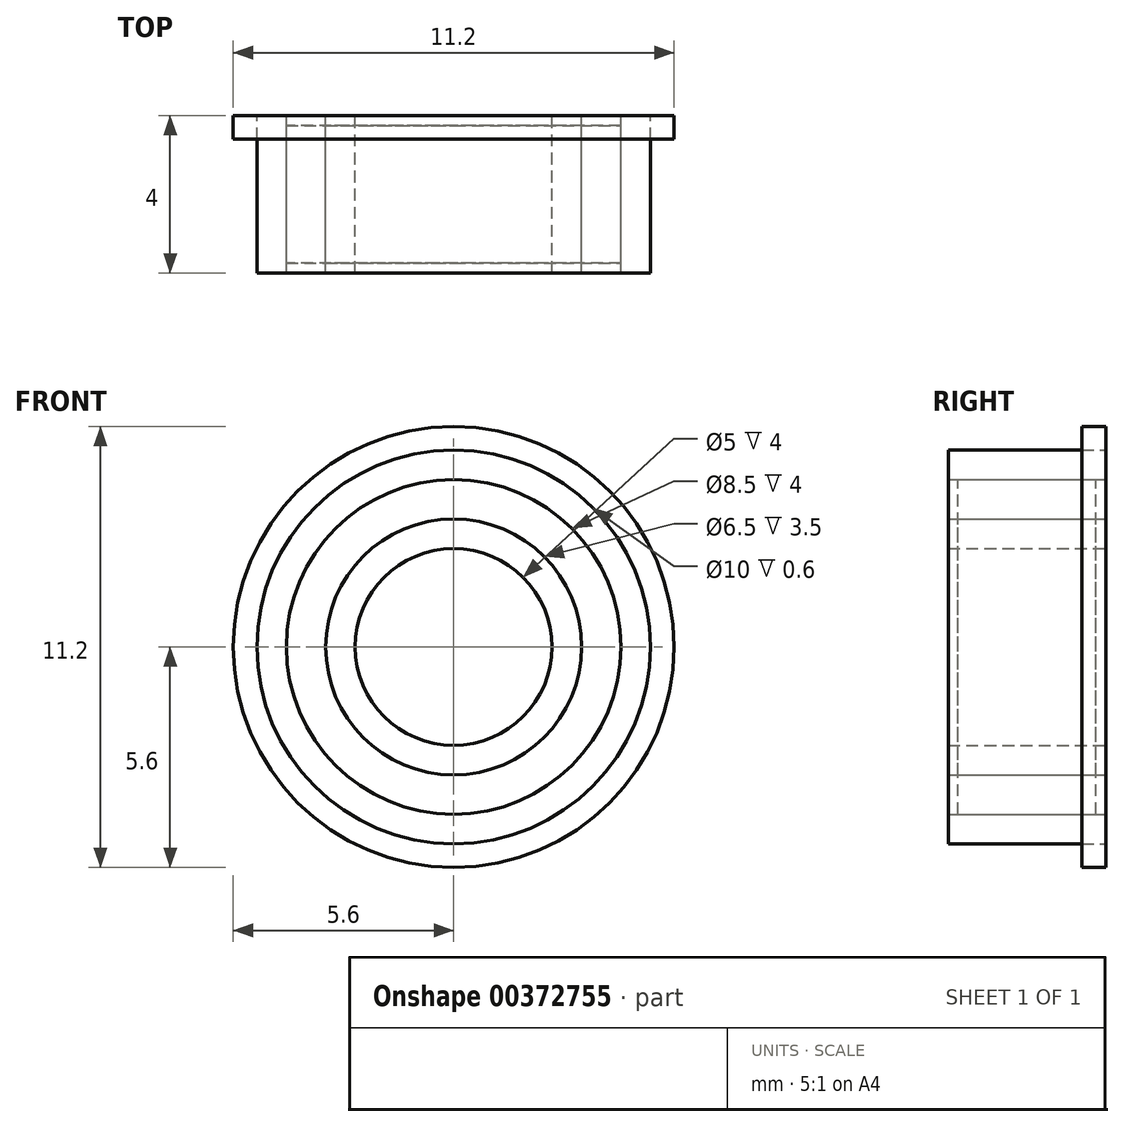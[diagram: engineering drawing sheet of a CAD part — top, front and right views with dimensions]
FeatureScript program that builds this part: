
annotation { "Feature Type Name" : "Feature", "Feature Type Description" : "" }
export const myFeature = defineFeature(function(context is Context, id is Id, definition is map)
    precondition{}
    {
        {
            assignVariable(context, id + "F0", {"name" : "B", "anyValue" : 4});
        }
        {
            assignVariable(context, id + "F1", {"name" : "C1", "anyValue" : 0.6});
        }
        {
            var Q0;
            Q0=qCreatedBy(makeId("Front.planeOp"),FACE);
            var sketch = newSketch(context, id + "F2", { "sketchPlane" : qUnion([Q0])});
            skCircle(sketch, "E0", {"center": v(0, 0) * mm, "radius": 5.6 * mm});
            skCircle(sketch, "E1", {"center": v(0, 0) * mm, "radius": 5 * mm});
            skSolve(sketch);
        }
        {
            var Q0;
            Q0=qSketchRegion(id+"F2",true);
            extrude(context, id + "F3", {"entities" : qUnion([Q0]), "depth" : (getVariable(context, 'C1')) * mm});
        }
        {
            var Q0;
            Q0=qCreatedBy(makeId("Front.planeOp"),FACE);
            var sketch = newSketch(context, id + "F4", { "sketchPlane" : qUnion([Q0])});
            skCircle(sketch, "E2", {"center": v(0, 0) * mm, "radius": 5 * mm});
            skCircle(sketch, "E3", {"center": v(0, 0) * mm, "radius": 4.25 * mm});
            skSolve(sketch);
        }
        {
            var Q0;
            Q0=qSketchRegion(id+"F4",true);
            extrude(context, id + "F5", {"entities" : qUnion([Q0]), "depth" : (getVariable(context, 'B')) * mm});
        }
        {
            var Q0;
            Q0=qCreatedBy(makeId("Front.planeOp"),FACE);
            var sketch = newSketch(context, id + "F6", { "sketchPlane" : qUnion([Q0])});
            skCircle(sketch, "E4", {"center": v(0, 0) * mm, "radius": 2.5 * mm});
            skCircle(sketch, "E5", {"center": v(0, 0) * mm, "radius": 3.25 * mm});
            skSolve(sketch);
        }
        {
            var Q0;
            Q0=qSketchRegion(id+"F6",true);
            extrude(context, id + "F7", {"entities" : qUnion([Q0]), "operationType" : NewBodyOperationType.ADD, "depth" : (getVariable(context, 'B')) * mm});
        }
        {
            var Q0;
            Q0=qCreatedBy(makeId("Front.planeOp"),FACE);
            cPlane(context, id + "F8", {"entities" : qUnion([Q0]), "cplaneType" : CPlaneType.OFFSET, "offset" : (getVariable(context, 'B') / 2) * mm, "width" : 150 * mm, "height" : 150 * mm});
        }
        {
            var Q0;
            Q0=qCreatedBy(id+"F8.planeOp",FACE);
            var sketch = newSketch(context, id + "F9", { "sketchPlane" : qUnion([Q0])});
            skCircle(sketch, "E6", {"center": v(0, 0) * mm, "radius": 3.25 * mm});
            skCircle(sketch, "E7", {"center": v(0, 0) * mm, "radius": 4.25 * mm});
            skSolve(sketch);
        }
        {
            var Q0;
            Q0=qSketchRegion(id+"F9",true);
            extrude(context, id + "F10", {"entities" : qUnion([Q0]), "depth" : (getVariable(context, 'B') - 0.5) * mm, "symmetric" : true});
        }
    });
